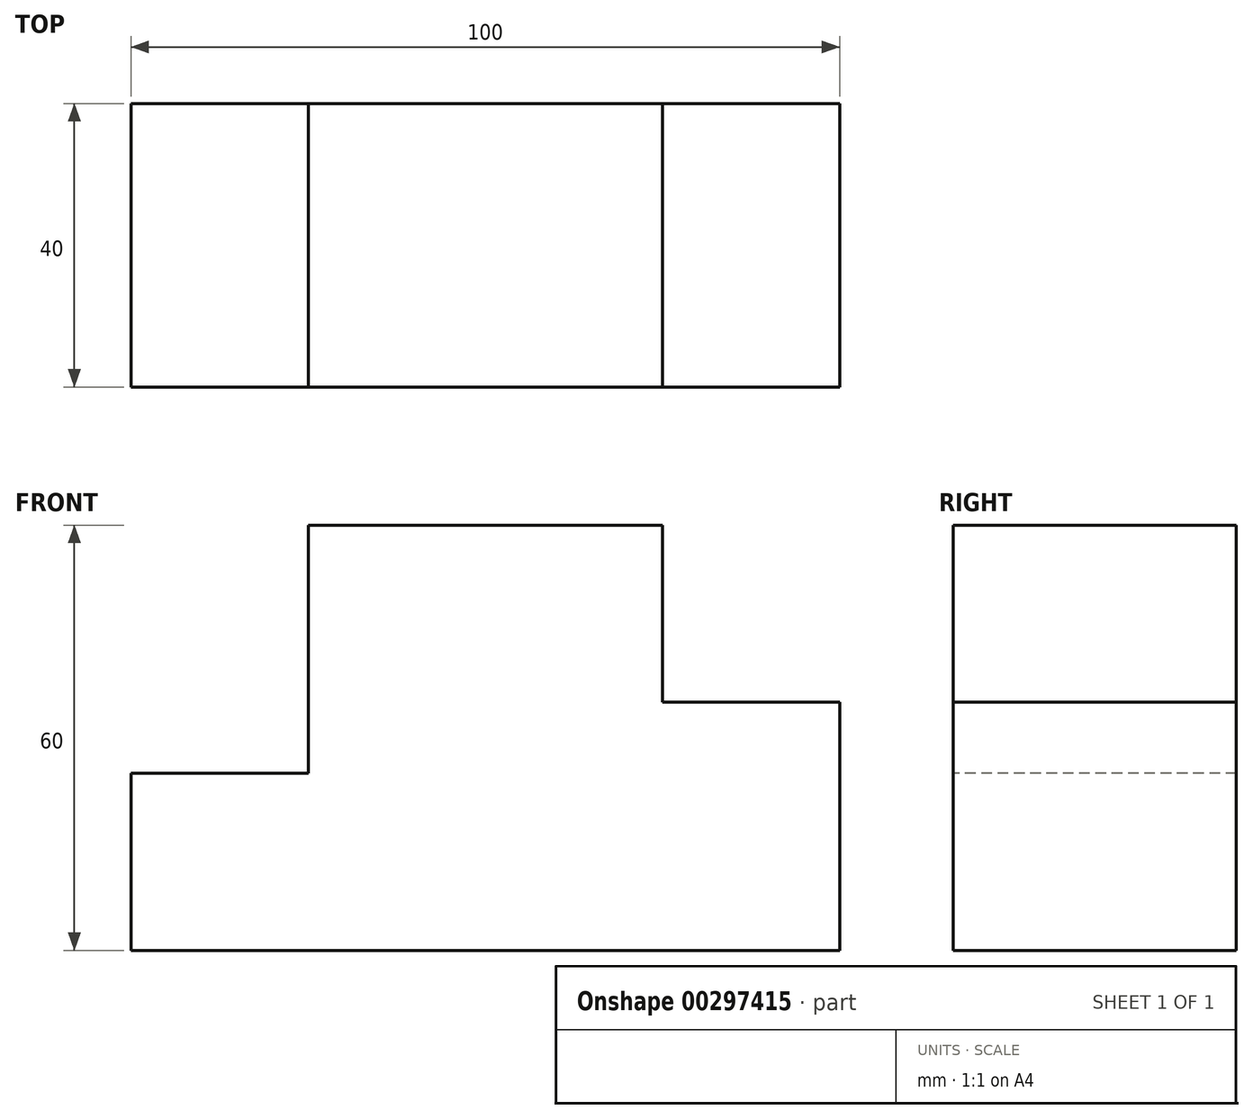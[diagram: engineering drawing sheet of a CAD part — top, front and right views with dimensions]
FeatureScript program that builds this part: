
annotation { "Feature Type Name" : "Feature", "Feature Type Description" : "" }
export const myFeature = defineFeature(function(context is Context, id is Id, definition is map)
    precondition{}
    {
        {
            var Q0;
            Q0=qCreatedBy(makeId("Front.planeOp"),FACE);
            var sketch = newSketch(context, id + "F0", { "sketchPlane" : qUnion([Q0])});
            skLineSegment(sketch, "E0.bottom", {"start": v(50, 30) * mm, "end": v(-50, 30) * mm});
            skLineSegment(sketch, "E0.top", {"start": v(50, -30) * mm, "end": v(-50, -30) * mm});
            skLineSegment(sketch, "E0.left", {"start": v(50, 30) * mm, "end": v(50, -30) * mm});
            skLineSegment(sketch, "E0.right", {"start": v(-50, 30) * mm, "end": v(-50, -30) * mm});
            skPoint(sketch, "E0.middle", {"position": v(0, 0) * mm});
            skSolve(sketch);
        }
        {
            var Q0;
            Q0=makeQuery(id+"F0.imprint","IMPRINT",FACE,{"disambiguationData":[TD([[makeQuery(id+"F0.imprint","IMPRINT",EDGE,{"derivedFrom":sQuery(id+"F0.wireOp",EDGE,"E0.bottom")}),1.0]])]});
            extrude(context, id + "F1", {"entities" : qUnion([Q0]), "depth" : 40 * mm});
        }
        {
            var Q0;
            Q0=makeQuery(id+"F1.opExtrude","CAP_FACE",FACE,{"disambiguationData":[OSD([sQuery(id+"F0.wireOp",EDGE,"E0.bottom"),sQuery(id+"F0.wireOp",EDGE,"E0.top"),sQuery(id+"F0.wireOp",EDGE,"E0.left"),sQuery(id+"F0.wireOp",EDGE,"E0.right")])],"isStart":false});
            var sketch = newSketch(context, id + "F2", { "sketchPlane" : qUnion([Q0])});
            skLineSegment(sketch, "E1.bottom", {"start": v(-50, 30) * mm, "end": v(-25, 30) * mm});
            skLineSegment(sketch, "E1.top", {"start": v(-50, -5) * mm, "end": v(-25, -5) * mm});
            skLineSegment(sketch, "E1.left", {"start": v(-50, 30) * mm, "end": v(-50, -5) * mm});
            skLineSegment(sketch, "E1.right", {"start": v(-25, 30) * mm, "end": v(-25, -5) * mm});
            skSolve(sketch);
        }
        {
            var Q0;
            Q0=makeQuery(id+"F2.imprint","IMPRINT",FACE,{"disambiguationData":[TD([[makeQuery(id+"F2.imprint","IMPRINT",EDGE,{"derivedFrom":sQuery(id+"F2.wireOp",EDGE,"E1.bottom")}),1.0]])]});
            extrude(context, id + "F3", {"entities" : qUnion([Q0]), "operationType" : NewBodyOperationType.REMOVE, "endBound" : BoundingType.THROUGH_ALL, "oppositeDirection" : true, "depth" : 25 * mm});
        }
        {
            var Q0;
            Q0=makeQuery(id+"F1.opExtrude","CAP_FACE",FACE,{"disambiguationData":[OSD([sQuery(id+"F0.wireOp",EDGE,"E0.bottom"),sQuery(id+"F0.wireOp",EDGE,"E0.top"),sQuery(id+"F0.wireOp",EDGE,"E0.left"),sQuery(id+"F0.wireOp",EDGE,"E0.right")])],"isStart":true});
            var sketch = newSketch(context, id + "F4", { "sketchPlane" : qUnion([Q0])});
            skLineSegment(sketch, "E2.bottom", {"start": v(-50, 30) * mm, "end": v(-25, 30) * mm});
            skLineSegment(sketch, "E2.top", {"start": v(-50, 5) * mm, "end": v(-25, 5) * mm});
            skLineSegment(sketch, "E2.left", {"start": v(-50, 30) * mm, "end": v(-50, 5) * mm});
            skLineSegment(sketch, "E2.right", {"start": v(-25, 30) * mm, "end": v(-25, 5) * mm});
            skSolve(sketch);
        }
        {
            var Q0;
            Q0=makeQuery(id+"F4.imprint","IMPRINT",FACE,{"disambiguationData":[TD([[makeQuery(id+"F4.imprint","IMPRINT",EDGE,{"derivedFrom":sQuery(id+"F4.wireOp",EDGE,"E2.bottom")}),-1.0]])]});
            extrude(context, id + "F5", {"entities" : qUnion([Q0]), "operationType" : NewBodyOperationType.REMOVE, "endBound" : BoundingType.THROUGH_ALL, "oppositeDirection" : true, "depth" : 25 * mm});
        }
    });
